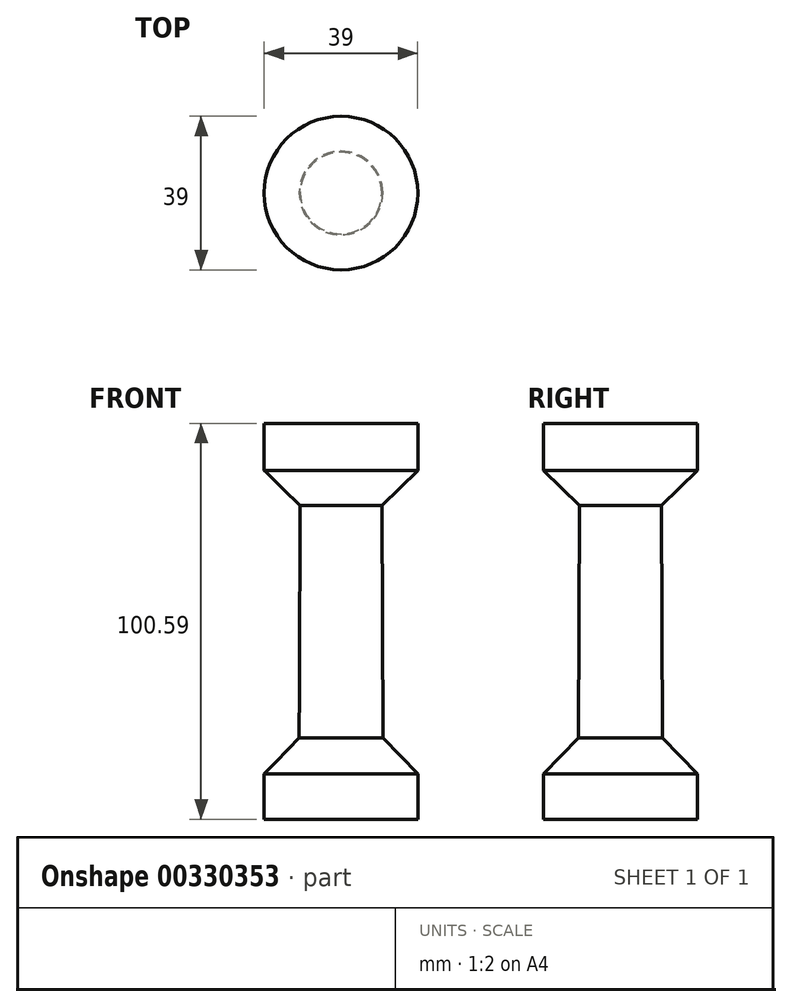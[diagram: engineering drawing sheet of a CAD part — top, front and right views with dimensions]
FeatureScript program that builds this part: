
annotation { "Feature Type Name" : "Feature", "Feature Type Description" : "" }
export const myFeature = defineFeature(function(context is Context, id is Id, definition is map)
    precondition{}
    {
        {
            var Q0;
            Q0=qCreatedBy(makeId("Front.planeOp"),FACE);
            var sketch = newSketch(context, id + "F0", { "sketchPlane" : qUnion([Q0])});
            skLineSegment(sketch, "E0", {"start": v(0, 0) * mm, "end": v(0, 47.99) * mm});
            skLineSegment(sketch, "E1", {"start": v(0, 47.99) * mm, "end": v(-19.5, 47.99) * mm});
            skLineSegment(sketch, "E2", {"start": v(-19.5, 47.99) * mm, "end": v(-19.5, 35.98) * mm});
            skLineSegment(sketch, "E3", {"start": v(-19.5, 35.98) * mm, "end": v(-10.38, 27.1) * mm});
            skLineSegment(sketch, "E4", {"start": v(-10.62, -31.95) * mm, "end": v(-10.38, 27.1) * mm});
            skLineSegment(sketch, "E5", {"start": v(-10.62, -31.95) * mm, "end": v(-19.5, -41.07) * mm});
            skLineSegment(sketch, "E6", {"start": v(-19.5, -41.07) * mm, "end": v(-19.5, -52.6) * mm});
            skLineSegment(sketch, "E7", {"start": v(-19.5, -52.6) * mm, "end": v(0, -52.6) * mm});
            skLineSegment(sketch, "E8", {"start": v(0, -52.6) * mm, "end": v(0, 0) * mm});
            skSolve(sketch);
        }
        {
            var Q0;
            Q0=makeQuery(id+"F0.imprint","IMPRINT",FACE,{"disambiguationData":[TD([[makeQuery(id+"F0.imprint","IMPRINT",EDGE,{"derivedFrom":sQuery(id+"F0.wireOp",EDGE,"E0")}),1.0]])]});
            var Q1;
            Q1=sQuery(id+"F0.wireOp",EDGE,"E0");
            revolve(context, id + "F1", {"entities" : qUnion([Q0]), "axis" : qUnion([Q1]), "revolveType" : RevolveType.FULL});
        }
    });
